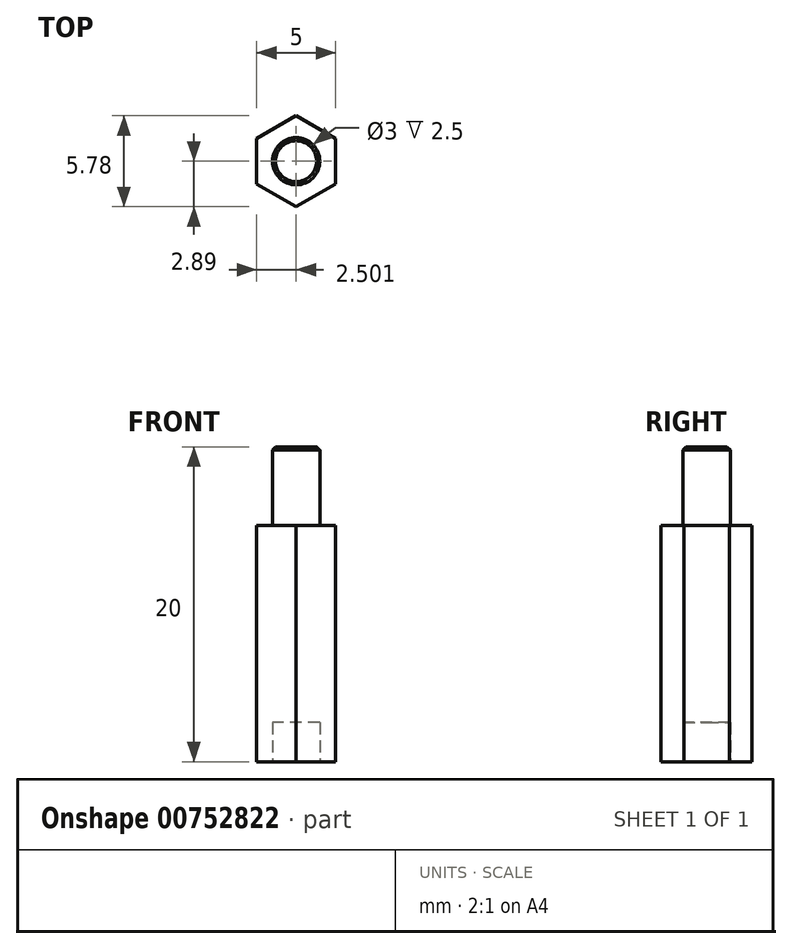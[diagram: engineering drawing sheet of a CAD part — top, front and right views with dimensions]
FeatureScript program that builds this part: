
annotation { "Feature Type Name" : "Feature", "Feature Type Description" : "" }
export const myFeature = defineFeature(function(context is Context, id is Id, definition is map)
    precondition{}
    {
        {
            var Q0;
            Q0=qCreatedBy(makeId("Top.planeOp"),FACE);
            var sketch = newSketch(context, id + "F0", { "sketchPlane" : qUnion([Q0])});
            skCircle(sketch, "E0.cCircle", {"center": v(-9.04, 0) * mm, "radius": 2.5 * mm, "construction": true});
            skLineSegment(sketch, "E0.0", {"start": v(-6.54, 1.44) * mm, "end": v(-6.54, -1.44) * mm});
            skLineSegment(sketch, "E0.1", {"start": v(-6.54, -1.44) * mm, "end": v(-9.04, -2.89) * mm});
            skLineSegment(sketch, "E0.2", {"start": v(-9.04, -2.89) * mm, "end": v(-11.54, -1.44) * mm});
            skLineSegment(sketch, "E0.3", {"start": v(-11.54, -1.44) * mm, "end": v(-11.54, 1.44) * mm});
            skLineSegment(sketch, "E0.4", {"start": v(-11.54, 1.44) * mm, "end": v(-9.04, 2.89) * mm});
            skLineSegment(sketch, "E0.5", {"start": v(-9.04, 2.89) * mm, "end": v(-6.54, 1.44) * mm});
            skPoint(sketch, "E0.0.midPoint", {"position": v(-6.54, 0) * mm});
            skCircle(sketch, "E1", {"center": v(-9.04, 0) * mm, "radius": 1.5 * mm});
            skSolve(sketch);
        }
        {
            var Q0;
            Q0=makeQuery(id+"F0.imprint","IMPRINT",FACE,{"disambiguationData":[TD([[makeQuery(id+"F0.imprint","IMPRINT",EDGE,{"derivedFrom":sQuery(id+"F0.wireOp",EDGE,"E0.0")}),-1.0]])]});
            var Q1;
            Q1=makeQuery(id+"F0.imprint","IMPRINT",FACE,{"disambiguationData":[TD([[makeQuery(id+"F0.imprint","IMPRINT",EDGE,{"derivedFrom":sQuery(id+"F0.wireOp",EDGE,"b4b620e1-f564-4398-8885-28afcf297faf.0")}),-1.0]])]});
            var Q2;
            Q2=makeQuery(id+"F0.imprint","IMPRINT",FACE,{"disambiguationData":[TD([[makeQuery(id+"F0.imprint","IMPRINT",EDGE,{"derivedFrom":sQuery(id+"F0.wireOp",EDGE,"b7cdad73-cb8f-43be-803a-25287b07029b.0")}),-1.0]])]});
            var Q3;
            Q3=makeQuery(id+"F0.imprint","IMPRINT",FACE,{"disambiguationData":[TD([[makeQuery(id+"F0.imprint","IMPRINT",EDGE,{"derivedFrom":sQuery(id+"F0.wireOp",EDGE,"bd8aa9ee-ead5-4eea-8d8e-92a14c97ab06.0")}),-1.0]])]});
            extrude(context, id + "F1", {"entities" : qUnion([Q0, Q1, Q2, Q3]), "depth" : 15 * mm, "offsetDistance" : 25 * mm});
        }
        {
            var Q0;
            Q0=makeQuery(id+"F0.imprint","IMPRINT",FACE,{"disambiguationData":[TD([[makeQuery(id+"F0.imprint","IMPRINT",EDGE,{"derivedFrom":sQuery(id+"F0.wireOp",EDGE,"E1")}),1.0]])]});
            var Q1;
            Q1=makeQuery(id+"F0.imprint","IMPRINT",FACE,{"disambiguationData":[TD([[makeQuery(id+"F0.imprint","IMPRINT",EDGE,{"derivedFrom":sQuery(id+"F0.wireOp",EDGE,"144471cf-6fd8-4119-b0d3-8bd12a2be911")}),1.0]])]});
            var Q2;
            Q2=makeQuery(id+"F0.imprint","IMPRINT",FACE,{"disambiguationData":[TD([[makeQuery(id+"F0.imprint","IMPRINT",EDGE,{"derivedFrom":sQuery(id+"F0.wireOp",EDGE,"a3026c50-73e1-403e-a0ed-a3fe235c9dc0")}),1.0]])]});
            var Q3;
            Q3=makeQuery(id+"F0.imprint","IMPRINT",FACE,{"disambiguationData":[TD([[makeQuery(id+"F0.imprint","IMPRINT",EDGE,{"derivedFrom":sQuery(id+"F0.wireOp",EDGE,"6d315694-e58b-4210-a824-2216d8d17368")}),1.0]])]});
            extrude(context, id + "F2", {"entities" : qUnion([Q0, Q1, Q2, Q3]), "operationType" : NewBodyOperationType.ADD, "depth" : 20 * mm, "offsetDistance" : 25 * mm});
        }
        {
            var Q0;
            Q0=makeQuery(id+"F2.opExtrude","CAP_EDGE",EDGE,{"disambiguationData":[OSD([sQuery(id+"F0.wireOp",EDGE,"E1")])],"isStart":false});
            var Q1;
            Q1=makeQuery(id+"F2.opExtrude","CAP_EDGE",EDGE,{"disambiguationData":[OSD([sQuery(id+"F0.wireOp",EDGE,"144471cf-6fd8-4119-b0d3-8bd12a2be911")])],"isStart":false});
            var Q2;
            Q2=makeQuery(id+"F2.opExtrude","CAP_EDGE",EDGE,{"disambiguationData":[OSD([sQuery(id+"F0.wireOp",EDGE,"a3026c50-73e1-403e-a0ed-a3fe235c9dc0")])],"isStart":false});
            var Q3;
            Q3=makeQuery(id+"F2.opExtrude","CAP_EDGE",EDGE,{"disambiguationData":[OSD([sQuery(id+"F0.wireOp",EDGE,"6d315694-e58b-4210-a824-2216d8d17368")])],"isStart":false});
            chamfer(context, id + "F3", {"entities" : qUnion([Q0, Q1, Q2, Q3]), "width" : 0.2 * mm, "tangentPropagation" : true});
        }
        {
            var Q0;
            Q0=makeQuery(id+"F0.imprint","IMPRINT",FACE,{"disambiguationData":[TD([[makeQuery(id+"F0.imprint","IMPRINT",EDGE,{"derivedFrom":sQuery(id+"F0.wireOp",EDGE,"a3026c50-73e1-403e-a0ed-a3fe235c9dc0")}),1.0]])]});
            var Q1;
            Q1=makeQuery(id+"F0.imprint","IMPRINT",FACE,{"disambiguationData":[TD([[makeQuery(id+"F0.imprint","IMPRINT",EDGE,{"derivedFrom":sQuery(id+"F0.wireOp",EDGE,"6d315694-e58b-4210-a824-2216d8d17368")}),1.0]])]});
            var Q2;
            Q2=makeQuery(id+"F0.imprint","IMPRINT",FACE,{"disambiguationData":[TD([[makeQuery(id+"F0.imprint","IMPRINT",EDGE,{"derivedFrom":sQuery(id+"F0.wireOp",EDGE,"E1")}),1.0]])]});
            var Q3;
            Q3=makeQuery(id+"F0.imprint","IMPRINT",FACE,{"disambiguationData":[TD([[makeQuery(id+"F0.imprint","IMPRINT",EDGE,{"derivedFrom":sQuery(id+"F0.wireOp",EDGE,"144471cf-6fd8-4119-b0d3-8bd12a2be911")}),1.0]])]});
            extrude(context, id + "F4", {"entities" : qUnion([Q0, Q1, Q2, Q3]), "operationType" : NewBodyOperationType.REMOVE, "depth" : 2.5 * mm, "offsetDistance" : 25 * mm});
        }
    });
